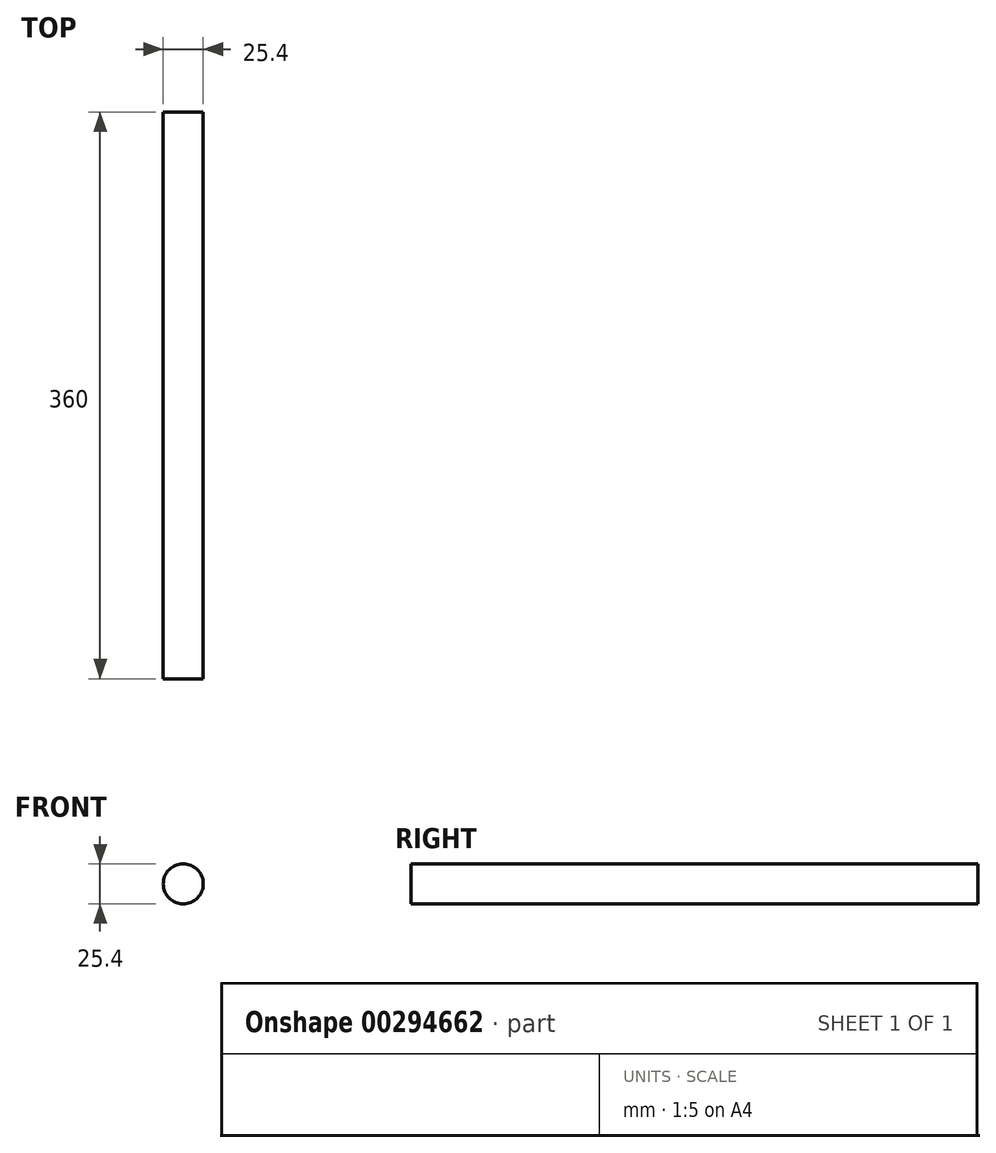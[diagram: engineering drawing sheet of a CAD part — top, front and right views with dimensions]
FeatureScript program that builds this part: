
annotation { "Feature Type Name" : "Feature", "Feature Type Description" : "" }
export const myFeature = defineFeature(function(context is Context, id is Id, definition is map)
    precondition{}
    {
        {
            var Q0;
            Q0=qCreatedBy(makeId("Front.planeOp"),FACE);
            var sketch = newSketch(context, id + "F0", { "sketchPlane" : qUnion([Q0])});
            skCircle(sketch, "E0", {"center": v(0, 0) * mm, "radius": 12.7 * mm});
            skSolve(sketch);
        }
        {
            var Q0;
            Q0 = qSketchRegion(id + "F0", true);
            extrude(context, id + "F1", {"entities" : qUnion([Q0]), "depth" : 360 * mm});
        }
    });
